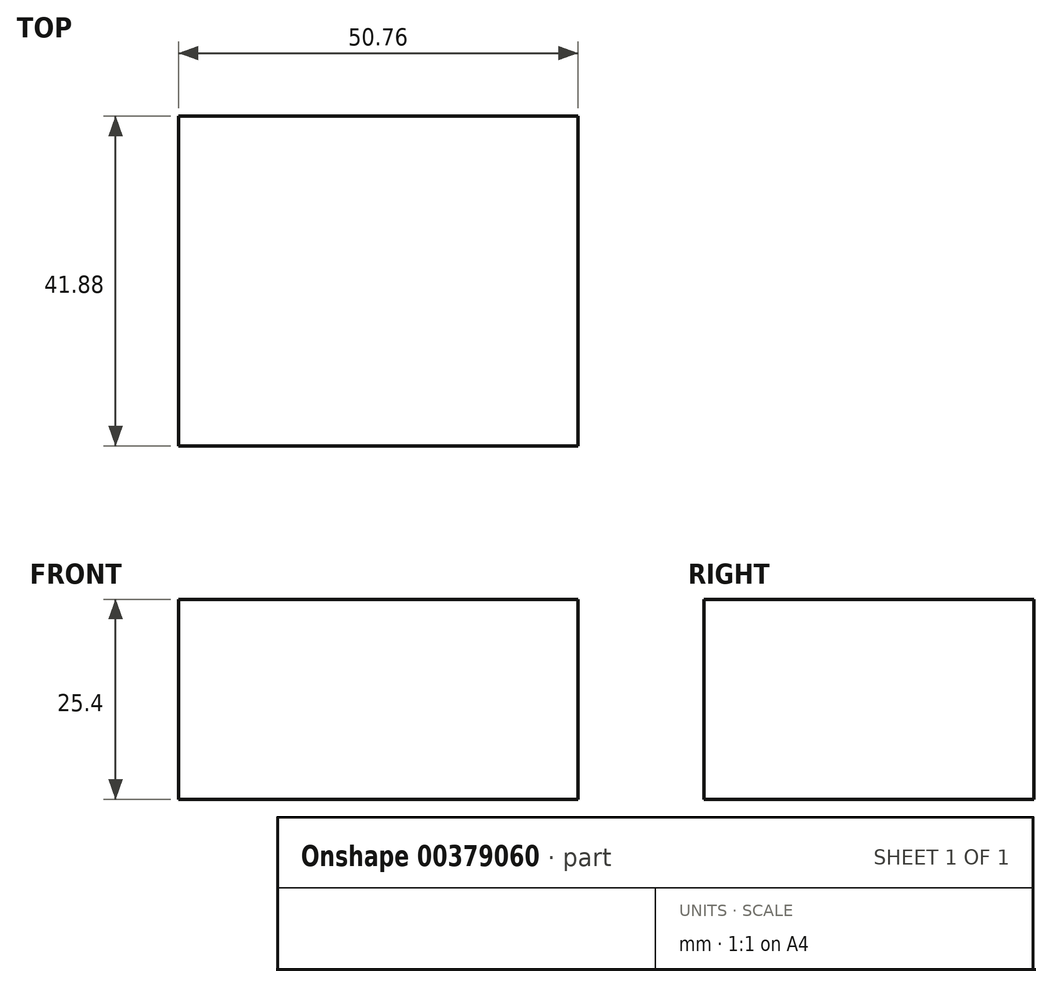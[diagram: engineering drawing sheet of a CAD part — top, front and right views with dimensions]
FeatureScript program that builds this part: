
annotation { "Feature Type Name" : "Feature", "Feature Type Description" : "" }
export const myFeature = defineFeature(function(context is Context, id is Id, definition is map)
    precondition{}
    {
        {
            var Q0;
            Q0=qCreatedBy(makeId("Top.planeOp"),FACE);
            var sketch = newSketch(context, id + "F0", { "sketchPlane" : qUnion([Q0])});
            skLineSegment(sketch, "E0.bottom", {"start": v(25.38, -20.94) * mm, "end": v(-25.38, -20.94) * mm});
            skLineSegment(sketch, "E0.top", {"start": v(25.38, 20.94) * mm, "end": v(-25.38, 20.94) * mm});
            skLineSegment(sketch, "E0.left", {"start": v(25.38, -20.94) * mm, "end": v(25.38, 20.94) * mm});
            skLineSegment(sketch, "E0.right", {"start": v(-25.38, -20.94) * mm, "end": v(-25.38, 20.94) * mm});
            skPoint(sketch, "E0.middle", {"position": v(0, 0) * mm});
            skSolve(sketch);
        }
        {
            var Q0;
            Q0=makeQuery(id+"F0.imprint","IMPRINT",FACE,{"disambiguationData":[TD([[makeQuery(id+"F0.imprint","IMPRINT",EDGE,{"derivedFrom":sQuery(id+"F0.wireOp",EDGE,"E0.bottom")}),-1.0]])]});
            extrude(context, id + "F1", {"entities" : qUnion([Q0]), "depth" : 25.4 * mm});
        }
    });
